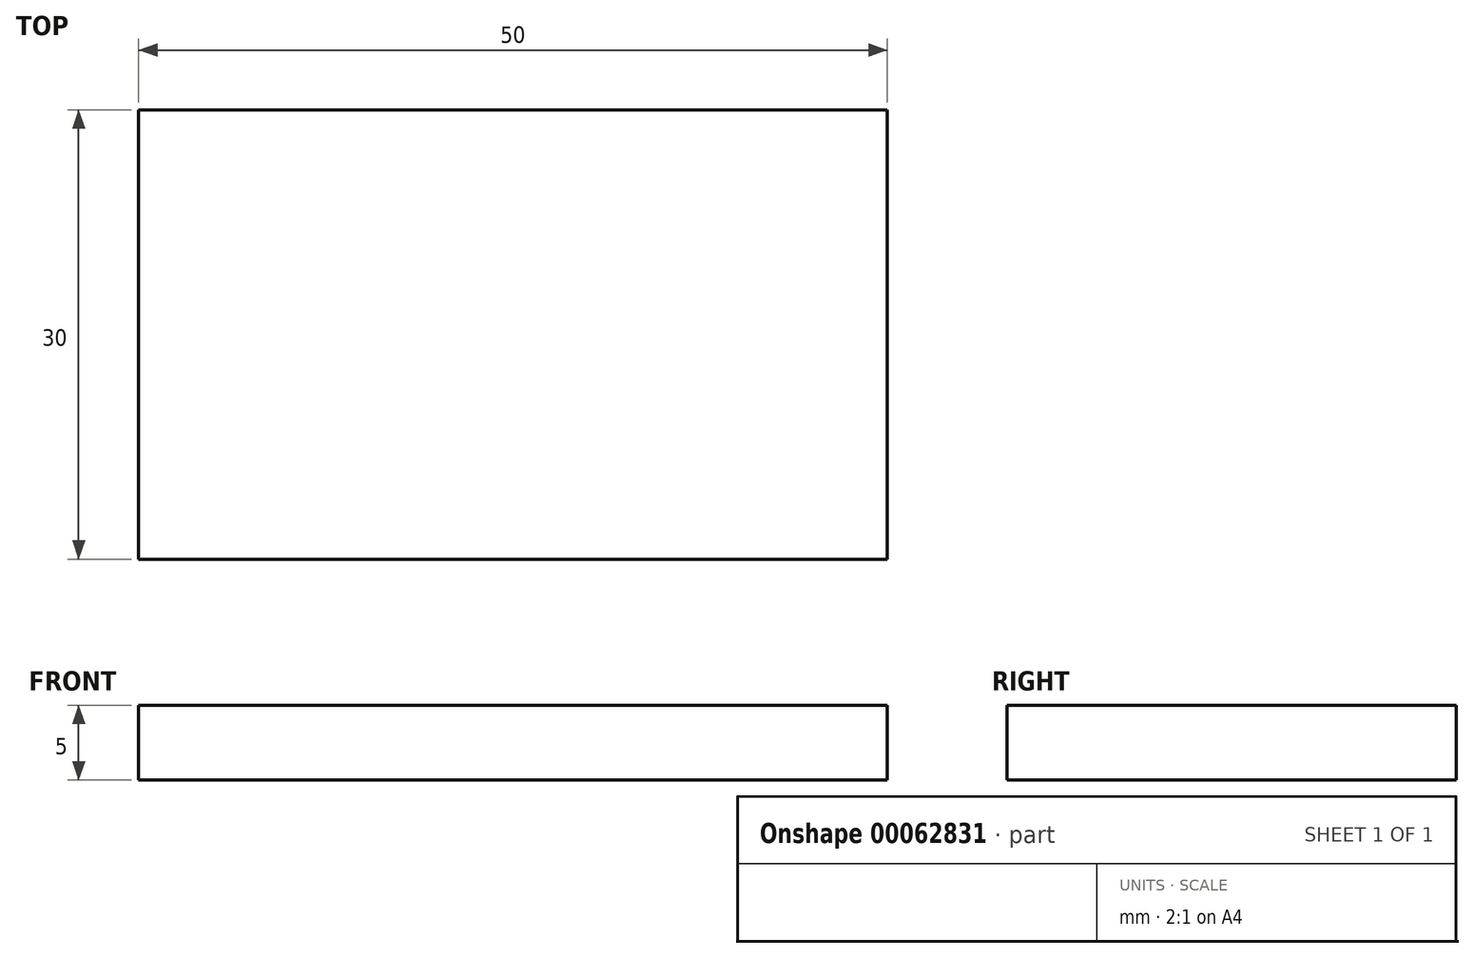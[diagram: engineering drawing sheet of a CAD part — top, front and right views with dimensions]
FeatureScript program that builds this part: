
annotation { "Feature Type Name" : "Feature", "Feature Type Description" : "" }
export const myFeature = defineFeature(function(context is Context, id is Id, definition is map)
    precondition{}
    {
        {
            var Q0;
            Q0=qCreatedBy(makeId("Top.planeOp"),FACE);
            var sketch = newSketch(context, id + "F0", { "sketchPlane" : qUnion([Q0])});
            skLineSegment(sketch, "E0.rect.bottom", {"start": v(25, 15) * mm, "end": v(-25, 15) * mm});
            skLineSegment(sketch, "E0.rect.top", {"start": v(25, -15) * mm, "end": v(-25, -15) * mm});
            skLineSegment(sketch, "E0.rect.left", {"start": v(25, 15) * mm, "end": v(25, -15) * mm});
            skLineSegment(sketch, "E0.rect.right", {"start": v(-25, 15) * mm, "end": v(-25, -15) * mm});
            skPoint(sketch, "E0.rect.middle", {"position": v(0, 0) * mm});
            skSolve(sketch);
        }
        {
            var Q0;
            Q0=makeQuery(id+"F0.imprint","IMPRINT",FACE,{"disambiguationData":[TD([[makeQuery(id+"F0.imprint","IMPRINT",EDGE,{"derivedFrom":sQuery(id+"F0.wireOp",EDGE,"E0.rect.bottom")}),1.0]])]});
            extrude(context, id + "F1", {"entities" : qUnion([Q0]), "depth" : 5 * mm});
        }
    });
